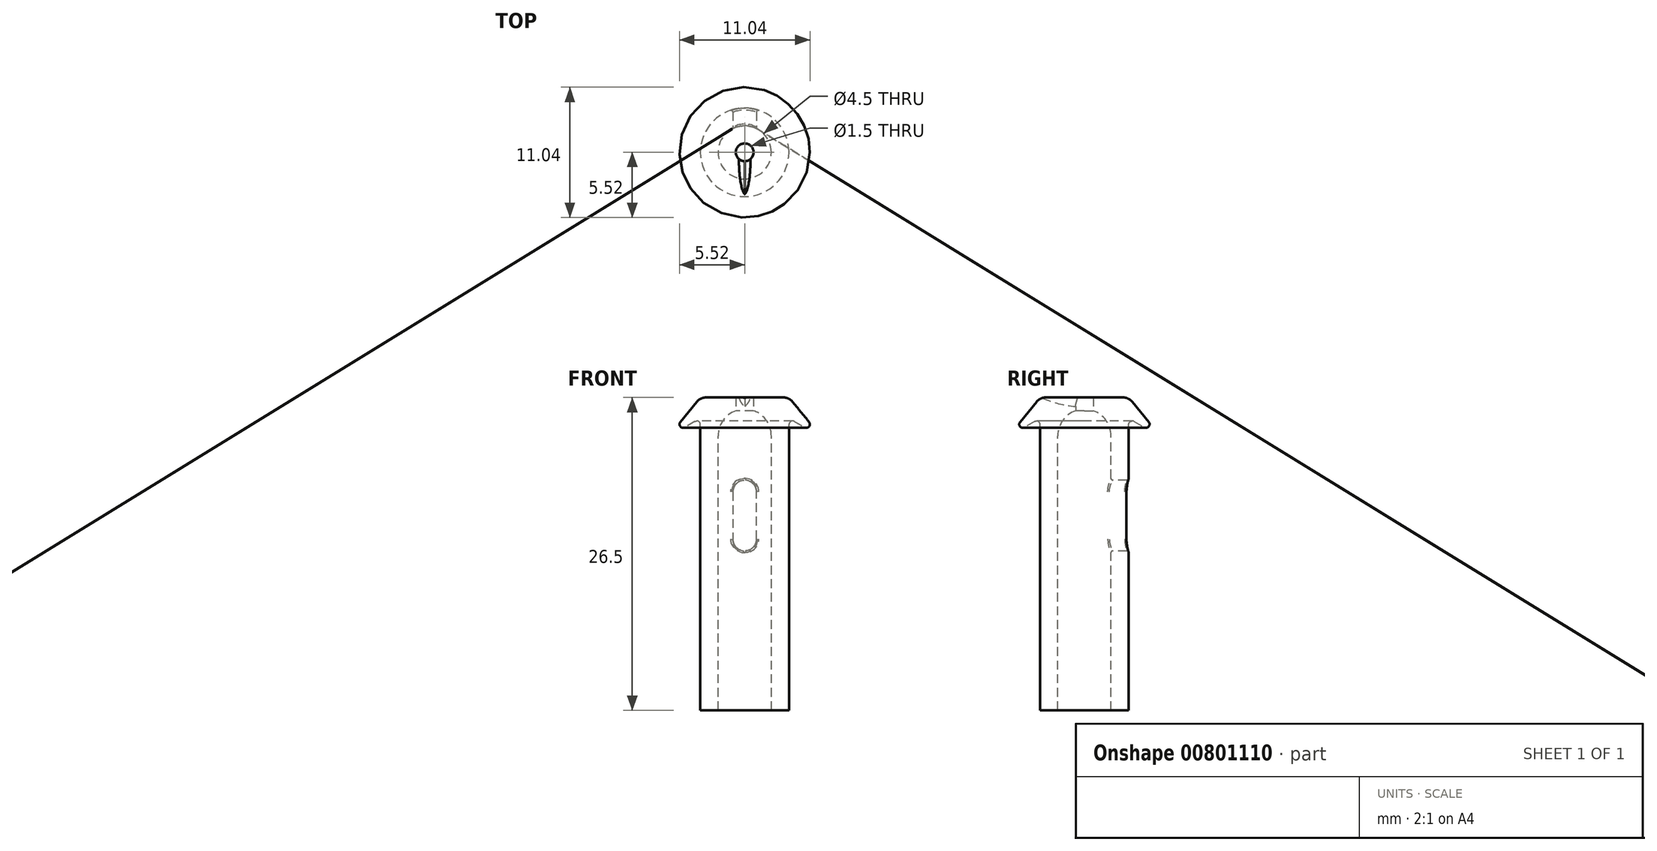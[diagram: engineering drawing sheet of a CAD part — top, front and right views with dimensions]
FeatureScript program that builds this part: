
annotation { "Feature Type Name" : "Feature", "Feature Type Description" : "" }
export const myFeature = defineFeature(function(context is Context, id is Id, definition is map)
    precondition{}
    {
        {
            var Q0;
            Q0=qCreatedBy(makeId("Front.planeOp"),FACE);
            var sketch = newSketch(context, id + "F0", { "sketchPlane" : qUnion([Q0])});
            skLineSegment(sketch, "E0", {"start": v(0, 10.59) * mm, "end": v(0, -11.76) * mm, "construction": true});
            skCircle(sketch, "E1", {"center": v(0, 0) * mm, "radius": 8.5 * mm, "construction": true});
            skCircle(sketch, "E2.0", {"center": v(0, 0) * mm, "radius": 8.2 * mm, "construction": true});
            skLineSegment(sketch, "E3", {"start": v(-3.75, 10) * mm, "end": v(0, 10) * mm});
            skLineSegment(sketch, "E4", {"start": v(-2.25, 0) * mm, "end": v(-2.25, 6.75) * mm});
            skArc(sketch, "E5", {"start": v(0, 9) * mm, "mid": v(-1.6, 8.34) * mm, "end": v(-2.25, 6.75) * mm});
            skLineSegment(sketch, "E6", {"start": v(-3.75, 7.7) * mm, "end": v(-3.75, 0) * mm});
            skLineSegment(sketch, "E7", {"start": v(-4.2, 7.97) * mm, "end": v(-5.07, 7.47) * mm});
            skArc(sketch, "E8", {"start": v(-5.45, 7.92) * mm, "mid": v(-5.44, 7.53) * mm, "end": v(-5.07, 7.47) * mm});
            skArc(sketch, "E9", {"start": v(-3.75, 7.7) * mm, "mid": v(-3.9, 7.97) * mm, "end": v(-4.2, 7.97) * mm});
            skLineSegment(sketch, "E10", {"start": v(-3.75, 0) * mm, "end": v(-3.75, -16.5) * mm});
            skLineSegment(sketch, "E11", {"start": v(-2.25, 0) * mm, "end": v(-2.25, -16.5) * mm});
            skLineSegment(sketch, "E12", {"start": v(-2.25, -16.5) * mm, "end": v(-3.75, -16.5) * mm});
            skLineSegment(sketch, "E13", {"start": v(-5.45, 7.92) * mm, "end": v(-3.75, 10) * mm});
            skLineSegment(sketch, "E14", {"start": v(0, 10) * mm, "end": v(0, 9) * mm});
            skSolve(sketch);
        }
        {
            var Q0;
            Q0=qSketchRegion(id+"F0",true);
            var Q1;
            Q1=sQuery(id+"F0.wireOp",EDGE,"E0");
            revolve(context, id + "F1", {"surfaceOperationType" : NewSurfaceOperationType.NEW, "entities" : qUnion([Q0]), "axis" : qUnion([Q1]), "revolveType" : RevolveType.FULL});
        }
        {
            var Q0;
            Q0=qCreatedBy(makeId("Right.planeOp"),FACE);
            var sketch = newSketch(context, id + "F2", { "sketchPlane" : qUnion([Q0])});
            skLineSegment(sketch, "E15", {"start": v(0, 18.6) * mm, "end": v(0, 13.07) * mm, "construction": true});
            skArc(sketch, "E16", {"start": v(-6.89, 12.46) * mm, "mid": v(-3.8, 10.07) * mm, "end": v(0, 9.2) * mm});
            skSolve(sketch);
        }
        {
            var Q0;
            Q0=sQuery(id+"F2.wireOp",EDGE,"E16");
            var Q1;
            Q1=sQuery(id+"F2.wireOp",VERTEX,"E16.start");
            cPlane(context, id + "F3", {"entities" : qUnion([Q0, Q1]), "cplaneType" : CPlaneType.CURVE_POINT, "offset" : 25 * mm, "width" : 150 * mm, "height" : 150 * mm});
        }
        {
            var Q0;
            Q0=qCreatedBy(id+"F3.planeOp",FACE);
            var sketch = newSketch(context, id + "F4", { "sketchPlane" : qUnion([Q0])});
            skLineSegment(sketch, "E17", {"start": v(0.5, -4.14) * mm, "end": v(0, -4.14) * mm});
            skLineSegment(sketch, "E18", {"start": v(0, -5.51) * mm, "end": v(0, -3.91) * mm, "construction": true});
            skArc(sketch, "E19", {"start": v(0.5, -4.14) * mm, "mid": v(0.46, -3.32) * mm, "end": v(0, -2.64) * mm});
            skLineSegment(sketch, "E20.MirrorCS", {"start": v(-0.5, -4.14) * mm, "end": v(0, -4.14) * mm});
            skArc(sketch, "E21.MirrorCS", {"start": v(-0.5, -4.14) * mm, "mid": v(-0.46, -3.32) * mm, "end": v(0, -2.64) * mm});
            skSolve(sketch);
        }
        {
            var Q0;
            Q0=makeQuery(id+"F4.imprint","IMPRINT",FACE,{"disambiguationData":[TD([[makeQuery(id+"F4.imprint","IMPRINT",EDGE,{"derivedFrom":sQuery(id+"F4.wireOp",EDGE,"E17")}),-1.0]])]});
            var Q1;
            Q1=qConstructionFilter(qBodyType(qCreatedBy(id+"F2",EDGE),BodyType.WIRE),ConstructionObject.NO);
            sweep(context, id + "F5", {"operationType" : NewBodyOperationType.REMOVE, "profiles" : qUnion([Q0]), "path" : qUnion([Q1])});
        }
        {
            var Q0;
            Q0=qCreatedBy(makeId("Top.planeOp"),FACE);
            var sketch = newSketch(context, id + "F6", { "sketchPlane" : qUnion([Q0])});
            skCircle(sketch, "E22", {"center": v(0, 0) * mm, "radius": 0.75 * mm});
            skSolve(sketch);
        }
        {
            var Q0;
            Q0=qSketchRegion(id+"F6",true);
            extrude(context, id + "F7", {"entities" : qUnion([Q0]), "operationType" : NewBodyOperationType.REMOVE, "endBound" : BoundingType.THROUGH_ALL, "depth" : 25 * mm, "offsetDistance" : 25 * mm});
        }
        {
            var Q0;
            Q0=qCreatedBy(makeId("Front.planeOp"),FACE);
            var sketch = newSketch(context, id + "F8", { "sketchPlane" : qUnion([Q0])});
            skLineSegment(sketch, "E23", {"start": v(0, 2) * mm, "end": v(0, -2) * mm, "construction": true});
            skArc(sketch, "E24", {"start": v(1, 2) * mm, "mid": v(0, 3) * mm, "end": v(-1, 2) * mm});
            skArc(sketch, "E25", {"start": v(-1, -2) * mm, "mid": v(0, -3) * mm, "end": v(1, -2) * mm});
            skLineSegment(sketch, "E26", {"start": v(-1, 2) * mm, "end": v(-1, -2) * mm});
            skLineSegment(sketch, "E27", {"start": v(1, 2) * mm, "end": v(1, -2) * mm});
            skSolve(sketch);
        }
        {
            var Q0;
            Q0=qSketchRegion(id+"F8",true);
            extrude(context, id + "F9", {"entities" : qUnion([Q0]), "operationType" : NewBodyOperationType.REMOVE, "endBound" : BoundingType.THROUGH_ALL, "oppositeDirection" : true, "depth" : 25 * mm, "offsetDistance" : 25 * mm});
        }
        {
            var Q0;
            Q0=makeQuery(id+"F9.boolean.opBoolean","COPY",FACE,{"derivedFrom":makeQuery(id+"F9.opExtrude","SWEPT_FACE",FACE,{"disambiguationData":[OSD([sQuery(id+"F8.wireOp",EDGE,"E24")])]})});
            fillet(context, id + "F10", {"entities" : qUnion([Q0]), "radius" : 0.15 * mm, "tangentPropagation" : true, "allowEdgeOverflow" : false});
        }
        {
            var Q0;
            Q0=makeQuery(id+"F1.opRevolve","SWEPT_EDGE",EDGE,{"disambiguationData":[OSD([sQuery(id+"F0.wireOp",EDGE,"E3"),sQuery(id+"F0.wireOp",EDGE,"E13")])]});
            fillet(context, id + "F11", {"entities" : qUnion([Q0]), "radius" : 1 * mm, "tangentPropagation" : true, "allowEdgeOverflow" : false});
        }
    });
